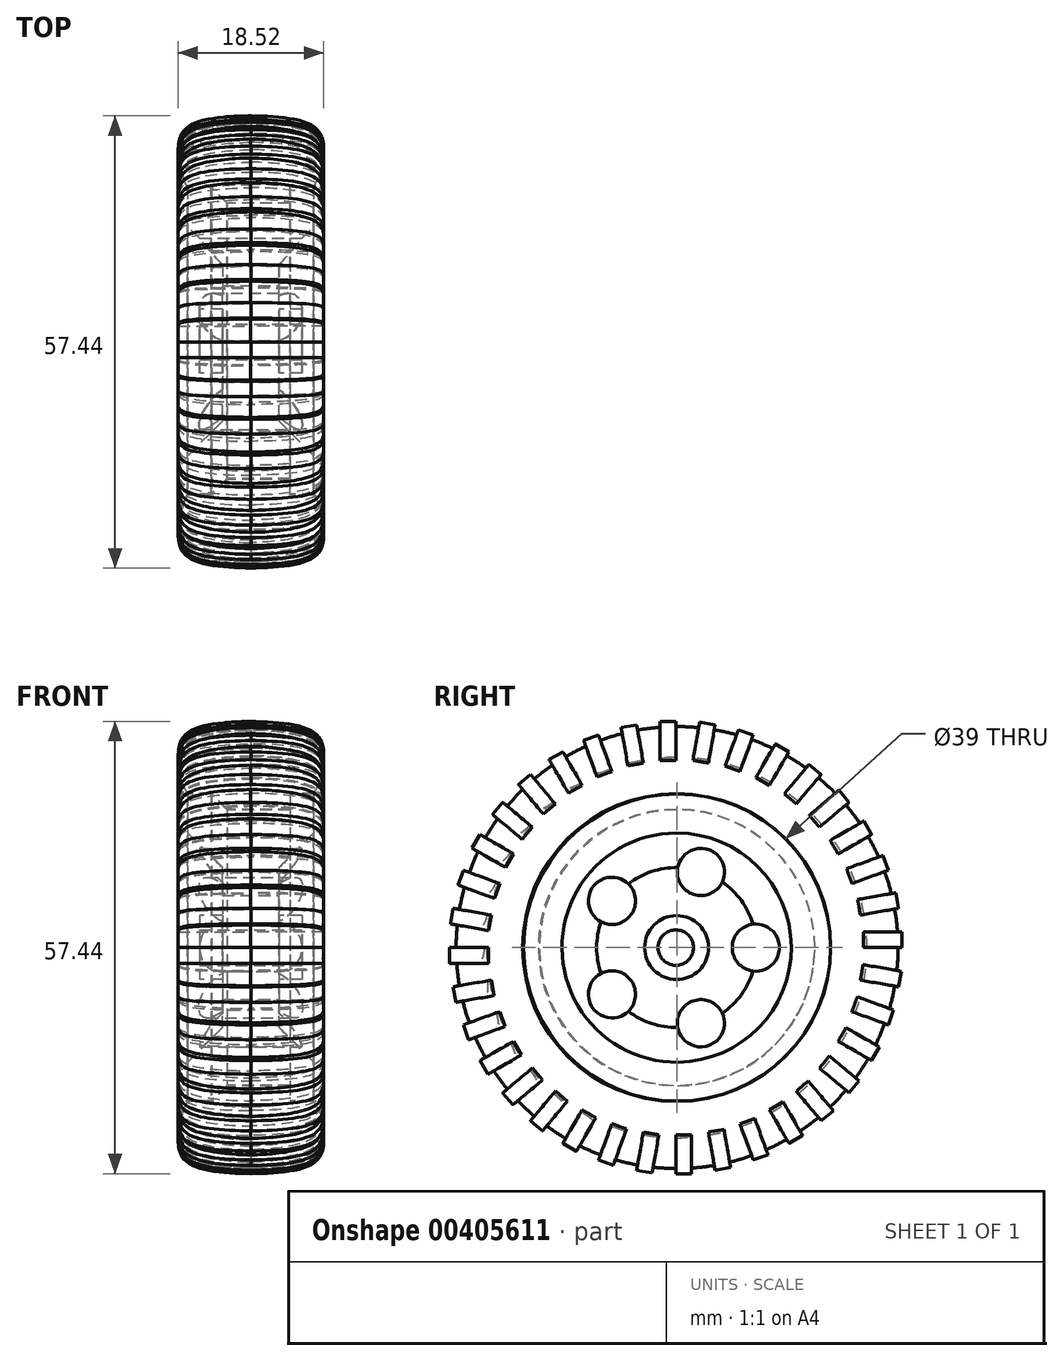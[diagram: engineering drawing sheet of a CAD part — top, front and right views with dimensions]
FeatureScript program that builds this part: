
annotation { "Feature Type Name" : "Feature", "Feature Type Description" : "" }
export const myFeature = defineFeature(function(context is Context, id is Id, definition is map)
    precondition{}
    {
        {
            var Q0;
            Q0=qCreatedBy(makeId("Top.planeOp"),FACE);
            var sketch = newSketch(context, id + "F0", { "sketchPlane" : qUnion([Q0])});
            skLineSegment(sketch, "E0", {"start": v(0, 0) * mm, "end": v(0, -5) * mm});
            skLineSegment(sketch, "E1", {"start": v(0, -5) * mm, "end": v(-4.4, -9.4) * mm});
            skLineSegment(sketch, "E2", {"start": v(-4.4, -9.4) * mm, "end": v(-4.4, -15.5) * mm});
            skLineSegment(sketch, "E3", {"start": v(-4.4, -15.5) * mm, "end": v(-1.5, -15.5) * mm});
            skLineSegment(sketch, "E4", {"start": v(-1.5, -15.5) * mm, "end": v(-1.5, -19.5) * mm});
            skLineSegment(sketch, "E5", {"start": v(-1.5, -19.5) * mm, "end": v(-14.5, -19.5) * mm});
            skLineSegment(sketch, "E6", {"start": v(-14.5, -19.5) * mm, "end": v(-14.5, -15.5) * mm});
            skLineSegment(sketch, "E7", {"start": v(-14.5, -15.5) * mm, "end": v(-11.6, -15.5) * mm});
            skLineSegment(sketch, "E8", {"start": v(-11.6, -15.5) * mm, "end": v(-11.6, -9.4) * mm});
            skLineSegment(sketch, "E9", {"start": v(-11.6, -9.4) * mm, "end": v(-16, -5) * mm});
            skLineSegment(sketch, "E10", {"start": v(-16, -5) * mm, "end": v(-16, 0) * mm});
            skLineSegment(sketch, "E11", {"start": v(-16, 0) * mm, "end": v(-13, 0) * mm});
            skLineSegment(sketch, "E12", {"start": v(-13, 0) * mm, "end": v(-11, -2) * mm});
            skLineSegment(sketch, "E13", {"start": v(-11, -2) * mm, "end": v(-3, -2) * mm});
            skLineSegment(sketch, "E14", {"start": v(-3, -2) * mm, "end": v(-3, 0) * mm});
            skLineSegment(sketch, "E15", {"start": v(-3, 0) * mm, "end": v(0, 0) * mm});
            skLineSegment(sketch, "E16", {"start": v(12.63, -19.5) * mm, "end": v(-28.55, -19.5) * mm, "construction": true});
            skPoint(sketch, "E16.startSnap0", {"position": v(-8, -19.5) * mm});
            skSolve(sketch);
        }
        {
            var Q0;
            Q0=qCreatedBy(makeId("Right.planeOp"),FACE);
            var sketch = newSketch(context, id + "F1", { "sketchPlane" : qUnion([Q0])});
            skCircle(sketch, "E17", {"center": v(-19.56, 0) * mm, "radius": 1 * mm});
            skSolve(sketch);
        }
        {
            var Q0;
            Q0=makeQuery(id+"F0.imprint","IMPRINT",FACE,{"disambiguationData":[TD([[makeQuery(id+"F0.imprint","IMPRINT",EDGE,{"derivedFrom":sQuery(id+"F0.wireOp",EDGE,"E0")}),-1.0]])]});
            var Q1;
            Q1=sQuery(id+"F1.wireOp",EDGE,"E17");
            revolve(context, id + "F2", {"entities" : qUnion([Q0]), "axis" : qUnion([Q1]), "revolveType" : RevolveType.FULL});
        }
        {
            var Q0;
            Q0=qCreatedBy(makeId("Right.planeOp"),FACE);
            var sketch = newSketch(context, id + "F3", { "sketchPlane" : qUnion([Q0])});
            skCircle(sketch, "E18", {"center": v(-19.66, 0) * mm, "radius": 2.25 * mm});
            skSolve(sketch);
        }
        {
            var Q0;
            Q0=makeQuery(id+"F3.imprint","IMPRINT",FACE,{"disambiguationData":[TD([[makeQuery(id+"F3.imprint","IMPRINT",EDGE,{"derivedFrom":sQuery(id+"F3.wireOp",EDGE,"E18")}),1.0]])]});
            extrude(context, id + "F4", {"entities" : qUnion([Q0]), "operationType" : NewBodyOperationType.REMOVE, "oppositeDirection" : true, "depth" : 25 * mm});
        }
        {
            var Q0;
            Q0=qCreatedBy(makeId("Right.planeOp"),FACE);
            var sketch = newSketch(context, id + "F5", { "sketchPlane" : qUnion([Q0])});
            skCircle(sketch, "E19", {"center": v(-9.5, 0) * mm, "radius": 3 * mm});
            skCircle(sketch, "E20.1.0", {"center": v(-16.48, 9.61) * mm, "radius": 3 * mm});
            skCircle(sketch, "E20.2.0", {"center": v(-27.78, 5.94) * mm, "radius": 3 * mm});
            skCircle(sketch, "E20.3.0", {"center": v(-27.78, -5.94) * mm, "radius": 3 * mm});
            skCircle(sketch, "E20.4.0", {"center": v(-16.48, -9.61) * mm, "radius": 3 * mm});
            skPoint(sketch, "E20.center", {"position": v(-19.6, 0) * mm});
            skSolve(sketch);
        }
        {
            var Q0;
            Q0=makeQuery(id+"F5.imprint","IMPRINT",FACE,{"disambiguationData":[TD([[makeQuery(id+"F5.imprint","IMPRINT",EDGE,{"derivedFrom":sQuery(id+"F5.wireOp",EDGE,"E19")}),1.0]])]});
            var Q1;
            Q1=makeQuery(id+"F5.imprint","IMPRINT",FACE,{"disambiguationData":[TD([[makeQuery(id+"F5.imprint","IMPRINT",EDGE,{"derivedFrom":sQuery(id+"F5.wireOp",EDGE,"E20.2.0")}),1.0]])]});
            var Q2;
            Q2=makeQuery(id+"F5.imprint","IMPRINT",FACE,{"disambiguationData":[TD([[makeQuery(id+"F5.imprint","IMPRINT",EDGE,{"derivedFrom":sQuery(id+"F5.wireOp",EDGE,"E20.3.0")}),1.0]])]});
            var Q3;
            Q3=makeQuery(id+"F5.imprint","IMPRINT",FACE,{"disambiguationData":[TD([[makeQuery(id+"F5.imprint","IMPRINT",EDGE,{"derivedFrom":sQuery(id+"F5.wireOp",EDGE,"E20.4.0")}),1.0]])]});
            var Q4;
            Q4=makeQuery(id+"F5.imprint","IMPRINT",FACE,{"disambiguationData":[TD([[makeQuery(id+"F5.imprint","IMPRINT",EDGE,{"derivedFrom":sQuery(id+"F5.wireOp",EDGE,"E20.1.0")}),1.0]])]});
            extrude(context, id + "F6", {"entities" : qUnion([Q0, Q1, Q2, Q3, Q4]), "operationType" : NewBodyOperationType.REMOVE, "oppositeDirection" : true, "depth" : 25 * mm});
        }
        {
            var Q0;
            Q0=qCreatedBy(makeId("Top.planeOp"),FACE);
            var sketch = newSketch(context, id + "F7", { "sketchPlane" : qUnion([Q0])});
            skLineSegment(sketch, "E21", {"start": v(0, 0) * mm, "end": v(-3, 0) * mm});
            skLineSegment(sketch, "E22", {"start": v(-3, 0) * mm, "end": v(-3, -2) * mm});
            skLineSegment(sketch, "E23", {"start": v(-3, -2) * mm, "end": v(-11.01, -2) * mm});
            skLineSegment(sketch, "E24", {"start": v(-11.01, -2) * mm, "end": v(-13.01, 0) * mm});
            skLineSegment(sketch, "E25", {"start": v(-13.01, 0) * mm, "end": v(-16.01, 0) * mm});
            skPoint(sketch, "E26.startSnap0", {"position": v(-1.5, 0) * mm});
            skFitSpline(sketch, "E27.MirrorCS", {"points": [v(-16, 0) * mm, v(-16.84, 1.78) * mm, v(-17.16, 3.1) * mm, v(-17.21, 4.54) * mm, v(-16, 6.93) * mm, v(-8, 8.57) * mm], "startDerivative": vector(-6.26, 11.56) * mm, "endDerivative": vector(25.2, 0.46) * mm});
            skLineSegment(sketch, "E28", {"start": v(-8, 0) * mm, "end": v(-8, 12.18) * mm, "construction": true});
            skFitSpline(sketch, "E29.MirrorCS", {"points": [v(0, 0) * mm, v(0.84, 1.78) * mm, v(1.16, 3.1) * mm, v(1.21, 4.54) * mm, v(0, 6.93) * mm, v(-8, 8.57) * mm], "startDerivative": vector(6.26, 11.56) * mm, "endDerivative": vector(-25.2, 0.46) * mm});
            skLineSegment(sketch, "E30", {"start": v(-23.27, -19.5) * mm, "end": v(11.66, -19.5) * mm, "construction": true});
            skLineSegment(sketch, "E31", {"start": v(-8, 1.09) * mm, "end": v(-8, 11.34) * mm, "construction": true});
            skSolve(sketch);
        }
        {
            var Q0;
            Q0=makeQuery(id+"F7.imprint","IMPRINT",FACE,{"disambiguationData":[TD([[makeQuery(id+"F7.imprint","IMPRINT",EDGE,{"derivedFrom":sQuery(id+"F7.wireOp",EDGE,"E21")}),-1.0]])]});
            var Q1;
            Q1=qSketchRegion(id+"F9",true);
            var Q2;
            Q2=sQuery(id+"F7.wireOp",EDGE,"E30");
            revolve(context, id + "F8", {"entities" : qUnion([Q0, Q1]), "axis" : qUnion([Q2]), "revolveType" : RevolveType.FULL});
        }
        {
            var Q0;
            Q0=qCreatedBy(makeId("Top.planeOp"),FACE);
            var sketch = newSketch(context, id + "F9", { "sketchPlane" : qUnion([Q0])});
            skFitSpline(sketch, "E32.MirrorCS", {"points": [v(0.03, -0.5) * mm, v(0.87, 1.28) * mm, v(1.2, 2.6) * mm, v(1.25, 4.04) * mm, v(0.03, 6.43) * mm, v(-7.97, 7.8) * mm], "startDerivative": vector(6.26, 11.56) * mm, "endDerivative": vector(-25.2, 0.46) * mm});
            skFitSpline(sketch, "E33.MirrorCS", {"points": [v(-15.97, -0.5) * mm, v(-16.81, 1.28) * mm, v(-17.13, 2.6) * mm, v(-17.18, 4.04) * mm, v(-15.96, 6.43) * mm, v(-7.97, 7.8) * mm], "startDerivative": vector(-6.26, 11.56) * mm, "endDerivative": vector(25.2, 0.46) * mm});
            skFitSpline(sketch, "E34.MirrorCS", {"points": [v(0.03, 0.76) * mm, v(0.87, 2.54) * mm, v(1.2, 3.86) * mm, v(1.25, 5.3) * mm, v(0.03, 7.68) * mm, v(-7.97, 9.06) * mm], "startDerivative": vector(6.26, 11.56) * mm, "endDerivative": vector(-25.2, 0.46) * mm});
            skFitSpline(sketch, "E35.MirrorCS", {"points": [v(-15.97, 0.76) * mm, v(-16.81, 2.54) * mm, v(-17.13, 3.86) * mm, v(-17.18, 5.3) * mm, v(-15.96, 7.68) * mm, v(-7.97, 9.06) * mm], "startDerivative": vector(-6.26, 11.56) * mm, "endDerivative": vector(25.2, 0.46) * mm});
            skLineSegment(sketch, "E36", {"start": v(-15.97, -0.5) * mm, "end": v(-15.97, 0.76) * mm});
            skLineSegment(sketch, "E37", {"start": v(0.03, -0.5) * mm, "end": v(0.03, 0.76) * mm});
            skSolve(sketch);
        }
        {
            var Q0;
            {var subQ0=sQuery(id+"F9.wireOp",EDGE,"E33.MirrorCS");var subQ1=sQuery(id+"F9.wireOp",EDGE,"E32.MirrorCS");var subQ2=makeQuery(id+"F9.imprint","INTERSECT",VERTEX,{"derivedFrom":[subQ1,subQ0]});Q0=makeQuery(id+"F9.imprint","IMPRINT",FACE,{"disambiguationData":[TD([[makeQuery(id+"F9.imprint","IMPRINT",EDGE,{"disambiguationData":[TD([[subQ2,1.0]])],"derivedFrom":subQ1}),-1.0]])]});}
            extrude(context, id + "F10", {"entities" : qUnion([Q0]), "depth" : 2 * mm});
        }
        {
            var Q0;
            Q0=makeQuery(id+"F10.opExtrude","SWEPT_BODY",BODY,{"disambiguationData":[OSD([sQuery(id+"F9.wireOp",EDGE,"E32.MirrorCS"),sQuery(id+"F9.wireOp",EDGE,"E33.MirrorCS"),sQuery(id+"F9.wireOp",EDGE,"E34.MirrorCS"),sQuery(id+"F9.wireOp",EDGE,"E35.MirrorCS")])]});
            var Q1;
            Q1=makeQuery(id+"F4.boolean.opBoolean","INTERSECT",EDGE,{"derivedFrom":[makeQuery(id+"F2.opRevolve","SWEPT_FACE",FACE,{"disambiguationData":[OSD([sQuery(id+"F0.wireOp",EDGE,"E4")])]}),makeQuery(id+"F4.opExtrude","SWEPT_FACE",FACE,{"disambiguationData":[OSD([sQuery(id+"F3.wireOp",EDGE,"E18")])]})]});
            circularPattern(context, id + "F11", {"operationType" : NewBodyOperationType.ADD, "entities" : qUnion([Q0]), "axis" : qUnion([Q1]), "angle" : 360 * degree, "instanceCount" : 36, "equalSpace" : true});
        }
    });
